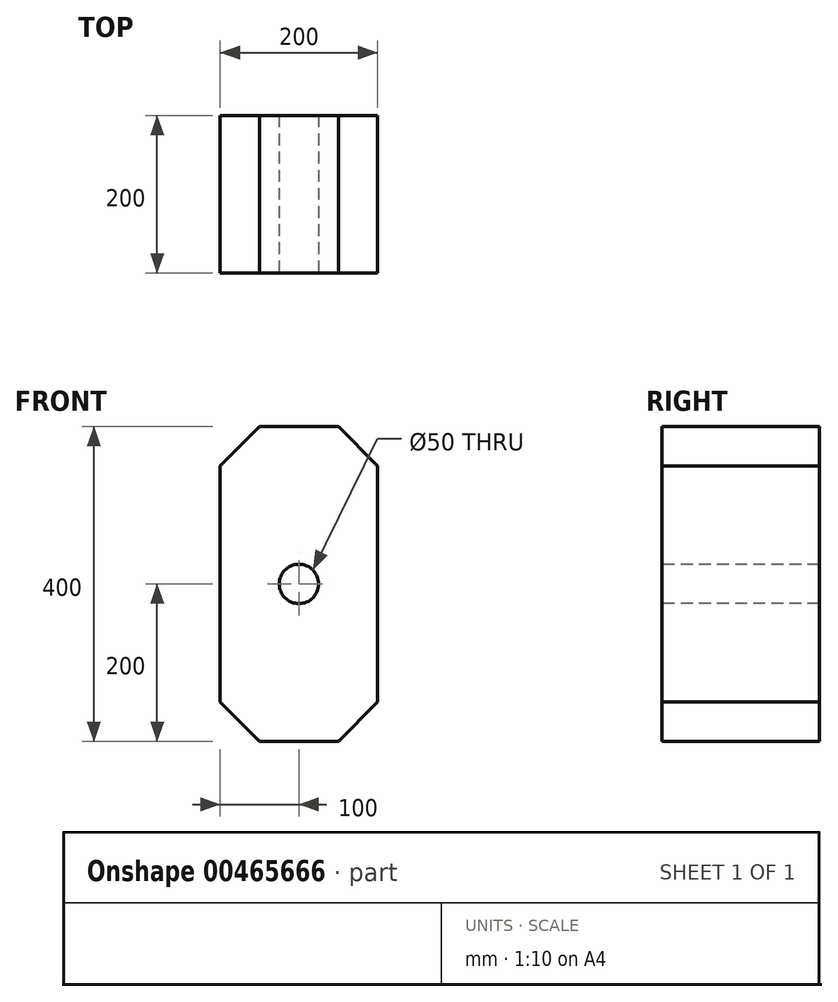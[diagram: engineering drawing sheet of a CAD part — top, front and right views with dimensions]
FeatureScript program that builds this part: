
annotation { "Feature Type Name" : "Feature", "Feature Type Description" : "" }
export const myFeature = defineFeature(function(context is Context, id is Id, definition is map)
    precondition{}
    {
        {
            var Q0;
            Q0=qCreatedBy(makeId("Front.planeOp"),FACE);
            var sketch = newSketch(context, id + "F0", { "sketchPlane" : qUnion([Q0])});
            skLineSegment(sketch, "E0.bottom", {"start": v(100, 200) * mm, "end": v(-100, 200) * mm});
            skLineSegment(sketch, "E0.top", {"start": v(100, -200) * mm, "end": v(-100, -200) * mm});
            skLineSegment(sketch, "E0.left", {"start": v(100, 200) * mm, "end": v(100, -200) * mm});
            skLineSegment(sketch, "E0.right", {"start": v(-100, 200) * mm, "end": v(-100, -200) * mm});
            skPoint(sketch, "E0.middle", {"position": v(0, 0) * mm});
            skSolve(sketch);
        }
        {
            var Q0;
            Q0=makeQuery(id+"F0.imprint","IMPRINT",FACE,{"disambiguationData":[TD([[makeQuery(id+"F0.imprint","IMPRINT",EDGE,{"derivedFrom":sQuery(id+"F0.wireOp",EDGE,"E0.bottom")}),1.0]])]});
            extrude(context, id + "F1", {"entities" : qUnion([Q0]), "depth" : 200 * mm});
        }
        {
            var Q0;
            Q0=makeQuery(id+"F1.opExtrude","CAP_FACE",FACE,{"disambiguationData":[OSD([sQuery(id+"F0.wireOp",EDGE,"E0.bottom"),sQuery(id+"F0.wireOp",EDGE,"E0.top"),sQuery(id+"F0.wireOp",EDGE,"E0.left"),sQuery(id+"F0.wireOp",EDGE,"E0.right")])],"isStart":false});
            var sketch = newSketch(context, id + "F2", { "sketchPlane" : qUnion([Q0])});
            skCircle(sketch, "E1", {"center": v(0, 0) * mm, "radius": 25 * mm});
            skSolve(sketch);
        }
        {
            var Q0;
            Q0=makeQuery(id+"F2.imprint","IMPRINT",FACE,{"disambiguationData":[TD([[makeQuery(id+"F2.imprint","IMPRINT",EDGE,{"derivedFrom":sQuery(id+"F2.wireOp",EDGE,"E1")}),1.0]])]});
            var Q1;
            Q1=sQuery(id+"F2.wireOp",EDGE,"E1");
            extrude(context, id + "F3", {"entities" : qUnion([Q0]), "operationType" : NewBodyOperationType.REMOVE, "surfaceEntities" : qUnion([Q1]), "endBound" : BoundingType.THROUGH_ALL, "oppositeDirection" : true, "depth" : 200 * mm});
        }
        {
            var Q0;
            Q0=makeQuery(id+"F1.opExtrude","SWEPT_EDGE",EDGE,{"disambiguationData":[OSD([sQuery(id+"F0.wireOp",EDGE,"E0.top"),sQuery(id+"F0.wireOp",EDGE,"E0.right")])]});
            chamfer(context, id + "F4", {"entities" : qUnion([Q0]), "width" : 50 * mm, "tangentPropagation" : true});
        }
        {
            var Q0;
            Q0=makeQuery(id+"F1.opExtrude","SWEPT_EDGE",EDGE,{"disambiguationData":[OSD([sQuery(id+"F0.wireOp",EDGE,"E0.top"),sQuery(id+"F0.wireOp",EDGE,"E0.left")])]});
            var Q1;
            Q1=makeQuery(id+"F1.opExtrude","SWEPT_EDGE",EDGE,{"disambiguationData":[OSD([sQuery(id+"F0.wireOp",EDGE,"E0.bottom"),sQuery(id+"F0.wireOp",EDGE,"E0.right")])]});
            var Q2;
            Q2=makeQuery(id+"F1.opExtrude","SWEPT_EDGE",EDGE,{"disambiguationData":[OSD([sQuery(id+"F0.wireOp",EDGE,"E0.bottom"),sQuery(id+"F0.wireOp",EDGE,"E0.left")])]});
            chamfer(context, id + "F5", {"entities" : qUnion([Q0, Q1, Q2]), "width" : 50 * mm, "tangentPropagation" : true});
        }
    });
